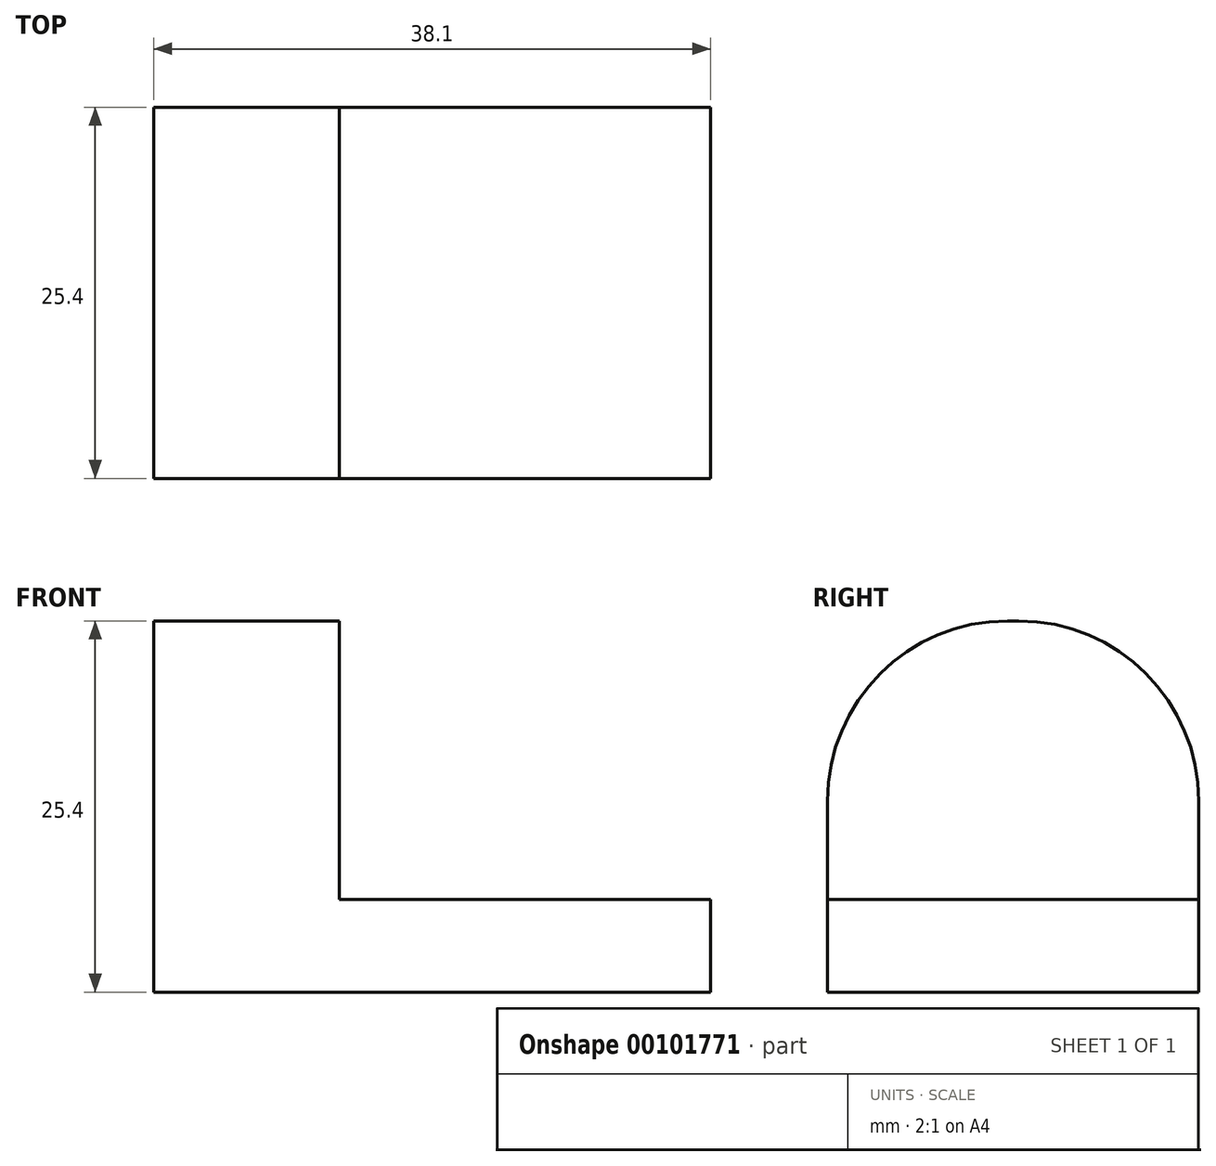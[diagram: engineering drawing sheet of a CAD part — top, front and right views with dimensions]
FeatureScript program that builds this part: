
annotation { "Feature Type Name" : "Feature", "Feature Type Description" : "" }
export const myFeature = defineFeature(function(context is Context, id is Id, definition is map)
    precondition{}
    {
        {
            var Q0;
            Q0=qCreatedBy(makeId("Front.planeOp"),FACE);
            var sketch = newSketch(context, id + "F0", { "sketchPlane" : qUnion([Q0])});
            skLineSegment(sketch, "E0.bottom", {"start": v(0, 0) * mm, "end": v(38.1, 0) * mm});
            skLineSegment(sketch, "E0.top", {"start": v(0, 25.4) * mm, "end": v(38.1, 25.4) * mm});
            skLineSegment(sketch, "E0.left", {"start": v(0, 0) * mm, "end": v(0, 25.4) * mm});
            skLineSegment(sketch, "E0.right", {"start": v(38.1, 0) * mm, "end": v(38.1, 25.4) * mm});
            skSolve(sketch);
        }
        {
            var Q0;
            Q0 = qSketchRegion(id + "F0", true);
            extrude(context, id + "F1", {"entities" : qUnion([Q0]), "endBound" : BoundingType.SYMMETRIC, "depth" : 25.4 * mm});
        }
        {
            var Q0;
            Q0=qCreatedBy(makeId("Front.planeOp"),FACE);
            var sketch = newSketch(context, id + "F2", { "sketchPlane" : qUnion([Q0])});
            skLineSegment(sketch, "E1", {"start": v(12.7, 25.4) * mm, "end": v(12.7, 6.35) * mm});
            skLineSegment(sketch, "E2", {"start": v(12.7, 6.35) * mm, "end": v(38.1, 6.35) * mm});
            skLineSegment(sketch, "E3", {"start": v(38.1, 6.35) * mm, "end": v(38.1, 25.4) * mm});
            skLineSegment(sketch, "E4", {"start": v(38.1, 25.4) * mm, "end": v(12.7, 25.4) * mm});
            skSolve(sketch);
        }
        {
            var Q0;
            Q0 = qSketchRegion(id + "F2", true);
            extrude(context, id + "F3", {"entities" : qUnion([Q0]), "operationType" : NewBodyOperationType.REMOVE, "endBound" : BoundingType.SYMMETRIC, "depth" : 25.4 * mm});
        }
        {
            var Q0;
            Q0=qCreatedBy(makeId("Right.planeOp"),FACE);
            var sketch = newSketch(context, id + "F4", { "sketchPlane" : qUnion([Q0])});
            skLineSegment(sketch, "E5", {"start": v(12.7, 12.7) * mm, "end": v(12.7, 13.07) * mm});
            skLineSegment(sketch, "E6", {"start": v(0.37, 25.4) * mm, "end": v(-0.37, 25.4) * mm});
            skLineSegment(sketch, "E7", {"start": v(-12.7, 13.07) * mm, "end": v(-12.7, 12.7) * mm});
            skPoint(sketch, "E8.visualSharp", {"position": v(12.7, 25.4) * mm});
            skArc(sketch, "E8.filletArc", {"start": v(12.7, 13.07) * mm, "mid": v(9.09, 21.79) * mm, "end": v(0.37, 25.4) * mm});
            skPoint(sketch, "E9.visualSharp", {"position": v(-12.7, 25.4) * mm});
            skArc(sketch, "E9.filletArc", {"start": v(-0.37, 25.4) * mm, "mid": v(-9.09, 21.79) * mm, "end": v(-12.7, 13.07) * mm});
            skLineSegment(sketch, "E10", {"start": v(12.7, 25.4) * mm, "end": v(12.7, 12.7) * mm});
            skLineSegment(sketch, "E11", {"start": v(12.7, 25.4) * mm, "end": v(0.37, 25.4) * mm});
            skLineSegment(sketch, "E12", {"start": v(-0.37, 25.4) * mm, "end": v(-12.7, 25.4) * mm});
            skLineSegment(sketch, "E13", {"start": v(-12.7, 12.7) * mm, "end": v(-12.7, 25.4) * mm});
            skSolve(sketch);
        }
        {
            var Q0;
            Q0 = qSketchRegion(id + "F4", true);
            extrude(context, id + "F5", {"entities" : qUnion([Q0]), "operationType" : NewBodyOperationType.REMOVE, "endBound" : BoundingType.SYMMETRIC, "depth" : 25.4 * mm});
        }
    });
